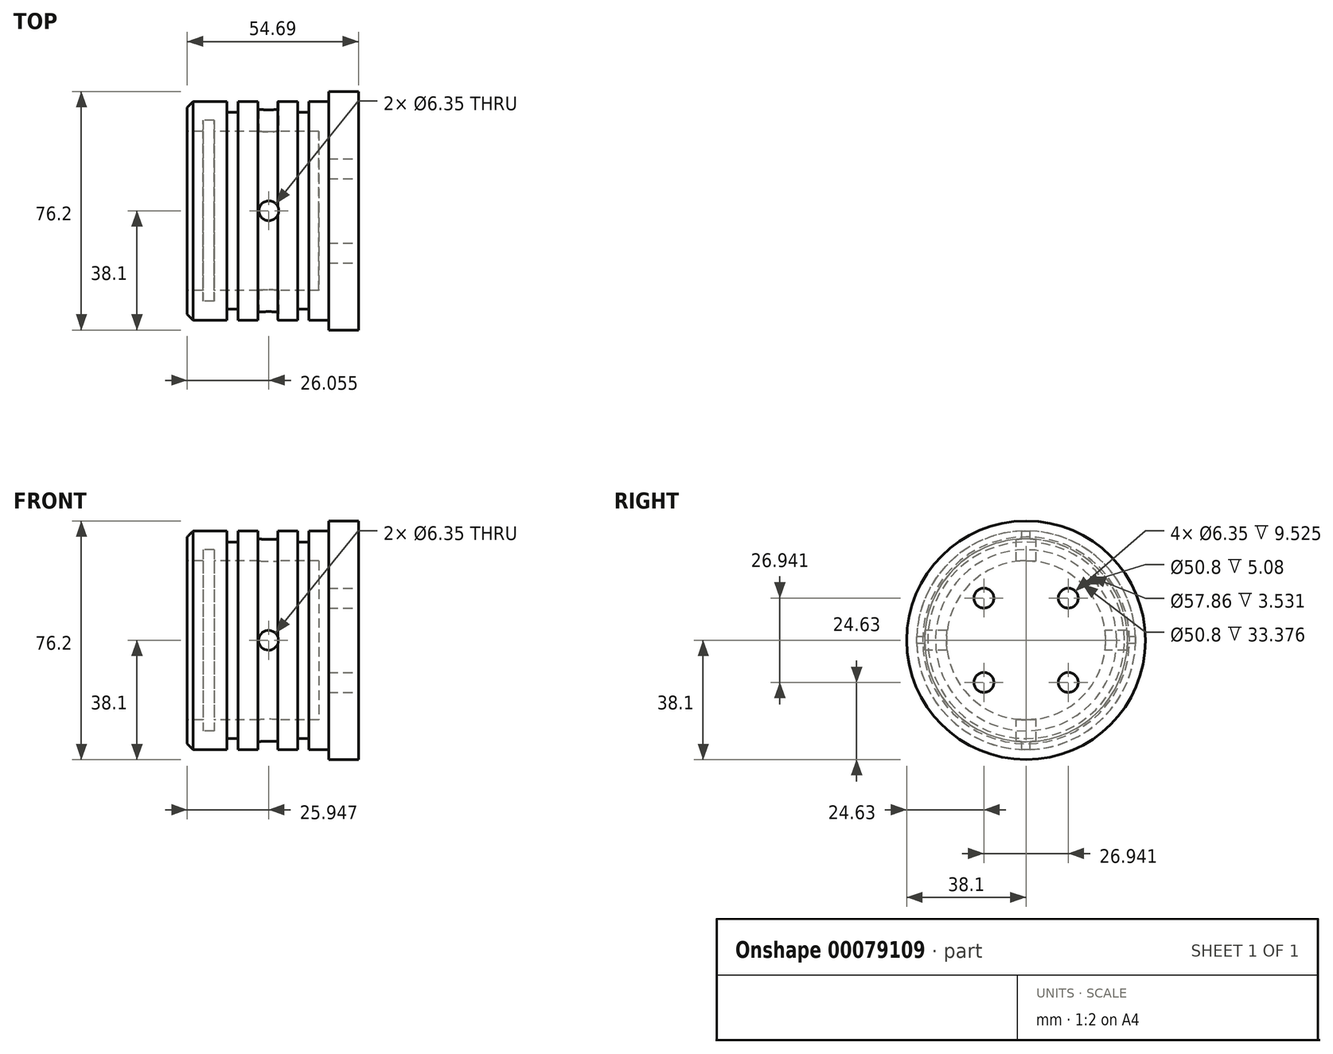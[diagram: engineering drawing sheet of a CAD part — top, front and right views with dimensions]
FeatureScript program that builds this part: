
annotation { "Feature Type Name" : "Feature", "Feature Type Description" : "" }
export const myFeature = defineFeature(function(context is Context, id is Id, definition is map)
    precondition{}
    {
        {
            var Q0;
            Q0=qCreatedBy(makeId("Front.planeOp"),FACE);
            var sketch = newSketch(context, id + "F0", { "sketchPlane" : qUnion([Q0])});
            skPoint(sketch, "E0.middle", {"position": v(0, 0) * mm});
            skLineSegment(sketch, "E1", {"start": v(-75.06, 0) * mm, "end": v(74.19, 0) * mm});
            skLineSegment(sketch, "E2", {"start": v(0, 25.4) * mm, "end": v(0, 34.93) * mm});
            skPoint(sketch, "E2.endSnap0", {"position": v(0, 25.4) * mm});
            skLineSegment(sketch, "E3", {"start": v(0, 34.93) * mm, "end": v(12.7, 34.93) * mm});
            skLineSegment(sketch, "E4", {"start": v(12.7, 34.93) * mm, "end": v(12.7, 31.4) * mm});
            skLineSegment(sketch, "E5", {"start": v(12.7, 31.4) * mm, "end": v(16.23, 31.4) * mm});
            skLineSegment(sketch, "E6", {"start": v(16.23, 31.4) * mm, "end": v(16.23, 34.93) * mm});
            skLineSegment(sketch, "E7", {"start": v(16.23, 34.93) * mm, "end": v(22.58, 34.93) * mm});
            skLineSegment(sketch, "E8", {"start": v(22.58, 34.93) * mm, "end": v(22.58, 32.39) * mm});
            skLineSegment(sketch, "E9", {"start": v(22.58, 32.39) * mm, "end": v(28.93, 32.39) * mm});
            skLineSegment(sketch, "E10", {"start": v(28.93, 32.39) * mm, "end": v(28.93, 34.93) * mm});
            skLineSegment(sketch, "E11", {"start": v(28.93, 34.93) * mm, "end": v(35.28, 34.93) * mm});
            skLineSegment(sketch, "E12", {"start": v(35.28, 34.93) * mm, "end": v(35.28, 31.4) * mm});
            skLineSegment(sketch, "E13", {"start": v(35.28, 31.4) * mm, "end": v(38.81, 31.4) * mm});
            skLineSegment(sketch, "E14", {"start": v(38.81, 31.4) * mm, "end": v(38.81, 34.93) * mm});
            skLineSegment(sketch, "E15", {"start": v(38.81, 34.93) * mm, "end": v(45.16, 34.93) * mm});
            skLineSegment(sketch, "E16", {"start": v(45.16, 34.93) * mm, "end": v(45.16, 38.1) * mm});
            skLineSegment(sketch, "E17", {"start": v(45.16, 38.1) * mm, "end": v(48.34, 38.1) * mm});
            skLineSegment(sketch, "E18", {"start": v(48.34, 38.1) * mm, "end": v(48.34, 25.53) * mm});
            skLineSegment(sketch, "E19", {"start": v(48.34, 25.53) * mm, "end": v(48.34, 0) * mm});
            skLineSegment(sketch, "E20", {"start": v(48.34, 0) * mm, "end": v(41.99, 0) * mm});
            skLineSegment(sketch, "E21", {"start": v(41.99, 0) * mm, "end": v(41.99, 25.4) * mm});
            skLineSegment(sketch, "E22", {"start": v(0, 25.4) * mm, "end": v(5.08, 25.4) * mm});
            skLineSegment(sketch, "E23", {"start": v(5.08, 25.4) * mm, "end": v(5.08, 28.93) * mm});
            skLineSegment(sketch, "E24", {"start": v(5.08, 28.93) * mm, "end": v(8.61, 28.93) * mm});
            skLineSegment(sketch, "E25", {"start": v(8.61, 28.93) * mm, "end": v(8.61, 25.4) * mm});
            skLineSegment(sketch, "E26", {"start": v(8.61, 25.4) * mm, "end": v(41.99, 25.4) * mm});
            skSolve(sketch);
        }
        {
            var Q0;
            Q0=makeQuery(id+"F0.imprint","IMPRINT",FACE,{"disambiguationData":[TD([[makeQuery(id+"F0.imprint","IMPRINT",EDGE,{"derivedFrom":sQuery(id+"F0.wireOp",EDGE,"E2")}),-1.0]])]});
            var Q1;
            Q1=sQuery(id+"F0.wireOp",EDGE,"E1");
            revolve(context, id + "F1", {"entities" : qUnion([Q0]), "axis" : qUnion([Q1]), "revolveType" : RevolveType.FULL});
        }
        {
            var Q0;
            Q0=qCreatedBy(makeId("Front.planeOp"),FACE);
            var sketch = newSketch(context, id + "F2", { "sketchPlane" : qUnion([Q0])});
            skCircle(sketch, "E27", {"center": v(25.95, 0) * mm, "radius": 3.18 * mm});
            skSolve(sketch);
        }
        {
            var Q0;
            Q0 = qSketchRegion(id + "F2", true);
            extrude(context, id + "F3", {"entities" : qUnion([Q0]), "operationType" : NewBodyOperationType.REMOVE, "endBound" : BoundingType.SYMMETRIC, "oppositeDirection" : true, "depth" : 76.2 * mm});
        }
        {
            var Q0;
            Q0=qCreatedBy(makeId("Top.planeOp"),FACE);
            var sketch = newSketch(context, id + "F4", { "sketchPlane" : qUnion([Q0])});
            skCircle(sketch, "E28", {"center": v(26.05, 0) * mm, "radius": 3.18 * mm});
            skSolve(sketch);
        }
        {
            var Q0;
            Q0=makeQuery(id+"F4.imprint","IMPRINT",FACE,{"disambiguationData":[TD([[makeQuery(id+"F4.imprint","IMPRINT",EDGE,{"derivedFrom":sQuery(id+"F4.wireOp",EDGE,"E28")}),1.0]])]});
            extrude(context, id + "F5", {"entities" : qUnion([Q0]), "operationType" : NewBodyOperationType.REMOVE, "endBound" : BoundingType.SYMMETRIC, "oppositeDirection" : true, "depth" : 76.2 * mm});
        }
        {
            var Q0;
            Q0=makeQuery(id+"F1.opRevolve","SWEPT_FACE",FACE,{"disambiguationData":[OSD([sQuery(id+"F0.wireOp",EDGE,"E18"),sQuery(id+"F0.wireOp",EDGE,"E19")])]});
            var sketch = newSketch(context, id + "F6", { "sketchPlane" : qUnion([Q0])});
            skSolve(sketch);
        }
        {
            var Q0;
            Q0=makeQuery(id+"F6.imprint","IMPRINT",FACE,{"disambiguationData":[TD([[makeQuery(id+"F6.imprint","IMPRINT",EDGE,{"derivedFrom":sQuery(id+"F6.wireOp",EDGE,"UFPXkMSn-KG9g-2dkP-bV8D-aUQ7KwiMVymJ")}),-1.0]])]});
            var Q1;
            Q1=makeQuery(id+"F1.opRevolve","SWEPT_FACE",FACE,{"disambiguationData":[OSD([sQuery(id+"F0.wireOp",EDGE,"E18"),sQuery(id+"F0.wireOp",EDGE,"E19")])]});
            extrude(context, id + "F7", {"entities" : qUnion([Q0, Q1]), "operationType" : NewBodyOperationType.ADD, "depth" : 6.35 * mm});
        }
        {
            var Q0;
            Q0=makeQuery(id+"F1.opRevolve","SWEPT_EDGE",EDGE,{"disambiguationData":[OSD([sQuery(id+"F0.wireOp",EDGE,"E2"),sQuery(id+"F0.wireOp",EDGE,"E3")])]});
            chamfer(context, id + "F8", {"entities" : qUnion([Q0]), "width" : 1.9 * mm, "tangentPropagation" : true});
        }
        {
            var Q0;
            Q0=makeQuery(id+"F7.opExtrude","CAP_FACE",FACE,{"disambiguationData":[OSD([sQuery(id+"F0.wireOp",EDGE,"E17"),sQuery(id+"F0.wireOp",EDGE,"E18"),sQuery(id+"F6.wireOp",EDGE,"UFPXkMSn-KG9g-2dkP-bV8D-aUQ7KwiMVymJ"),sQuery(id+"F6.wireOp",EDGE,"RpvYJHGx-UIbs-7FQv-in5p-XT8UD1pWvsJd"),sQuery(id+"F6.wireOp",EDGE,"5y3mjskV-gnoP-OKxi-8B2g-FI1IZNGVPEWQ")])],"isStart":false});
            var sketch = newSketch(context, id + "F9", { "sketchPlane" : qUnion([Q0])});
            skPoint(sketch, "E29.middle", {"position": v(0, 0) * mm});
            skCircle(sketch, "E30", {"center": v(13.47, 13.47) * mm, "radius": 3.18 * mm});
            skCircle(sketch, "E31", {"center": v(13.47, -13.47) * mm, "radius": 3.18 * mm});
            skCircle(sketch, "E32", {"center": v(-13.47, -13.47) * mm, "radius": 3.18 * mm});
            skCircle(sketch, "E33", {"center": v(-13.47, 13.47) * mm, "radius": 3.18 * mm});
            skSolve(sketch);
        }
        {
            var Q0;
            Q0 = qSketchRegion(id + "F9", true);
            extrude(context, id + "F10", {"entities" : qUnion([Q0]), "operationType" : NewBodyOperationType.REMOVE, "oppositeDirection" : true, "depth" : 9.52 * mm});
        }
    });
